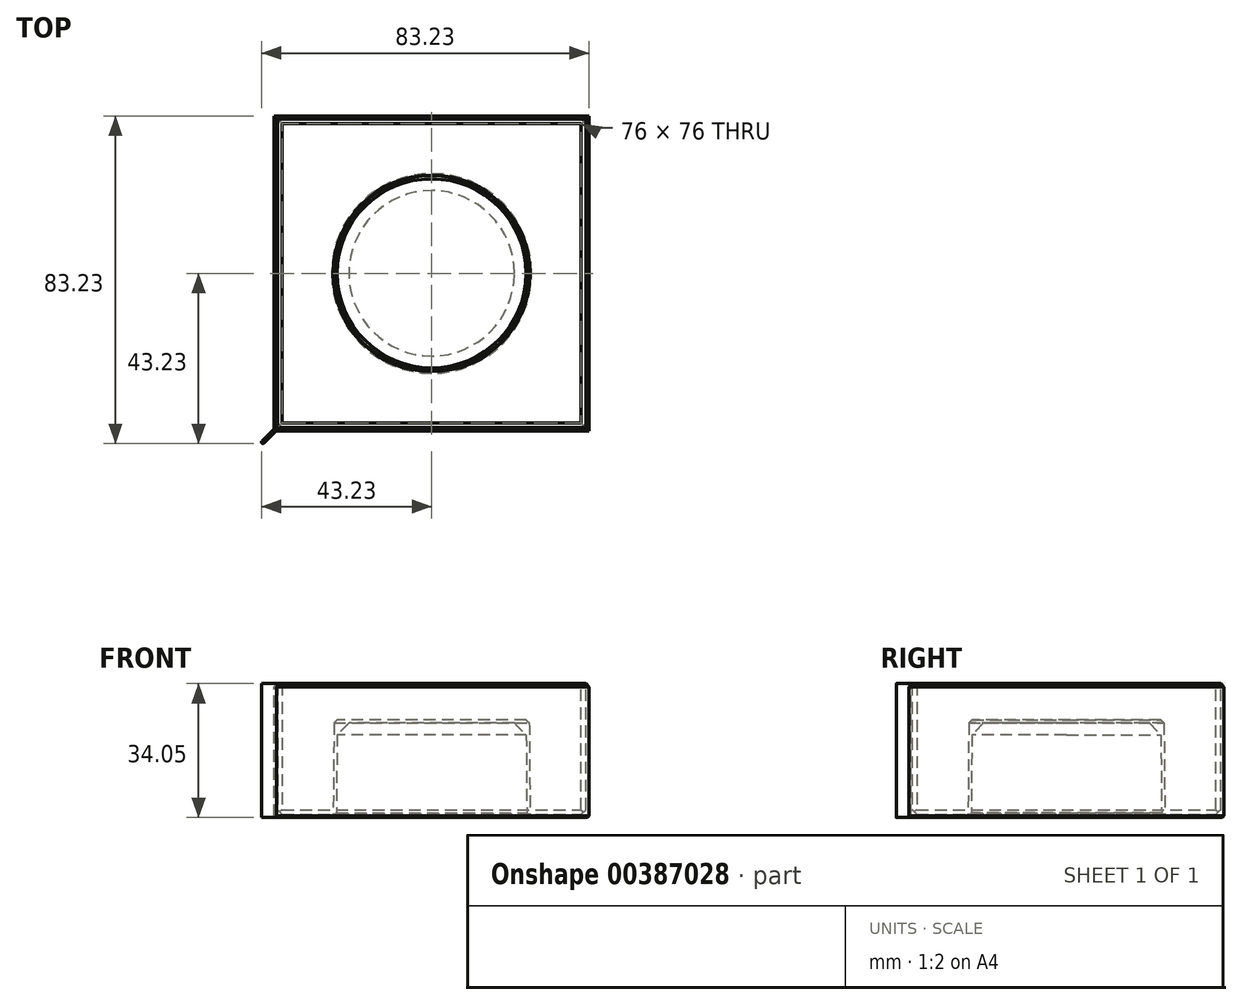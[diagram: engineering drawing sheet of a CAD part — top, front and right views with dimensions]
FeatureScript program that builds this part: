
annotation { "Feature Type Name" : "Feature", "Feature Type Description" : "" }
export const myFeature = defineFeature(function(context is Context, id is Id, definition is map)
    precondition{}
    {
        {
            var Q0;
            Q0=qCreatedBy(makeId("Top.planeOp"),FACE);
            var sketch = newSketch(context, id + "F0", { "sketchPlane" : qUnion([Q0])});
            skLineSegment(sketch, "E0.bottom", {"start": v(-40, 40) * mm, "end": v(40, 40) * mm});
            skLineSegment(sketch, "E0.top", {"start": v(-40, -40) * mm, "end": v(40, -40) * mm});
            skLineSegment(sketch, "E0.left", {"start": v(-40, 40) * mm, "end": v(-40, -40) * mm});
            skLineSegment(sketch, "E0.right", {"start": v(40, 40) * mm, "end": v(40, -40) * mm});
            skPoint(sketch, "E0.middle", {"position": v(0, 0) * mm});
            skSolve(sketch);
        }
        {
            var Q0;
            Q0 = qSketchRegion(id + "F0", true);
            extrude(context, id + "F1", {"entities" : qUnion([Q0]), "depth" : 34 * mm});
        }
        {
            var Q0;
            Q0=makeQuery(id+"F1.opExtrude","CAP_FACE",FACE,{"disambiguationData":[OSD([sQuery(id+"F0.wireOp",EDGE,"E0.bottom"),sQuery(id+"F0.wireOp",EDGE,"E0.top"),sQuery(id+"F0.wireOp",EDGE,"E0.left"),sQuery(id+"F0.wireOp",EDGE,"E0.right")])],"isStart":false});
            shell(context, id + "F2", {"entities" : qUnion([Q0]), "thickness" : 0.8 * mm});
        }
        {
            var Q0;
            Q0=makeQuery(id+"F2.opShell","OFFSET_FACE",FACE,{"disambiguationData":[OSD([sQuery(id+"F0.wireOp",EDGE,"E0.bottom"),sQuery(id+"F0.wireOp",EDGE,"E0.top"),sQuery(id+"F0.wireOp",EDGE,"E0.left"),sQuery(id+"F0.wireOp",EDGE,"E0.right")])]});
            var sketch = newSketch(context, id + "F3", { "sketchPlane" : qUnion([Q0])});
            skCircle(sketch, "E1", {"center": v(0, 0) * mm, "radius": 25 * mm});
            skSolve(sketch);
        }
        {
            var Q0;
            Q0 = qSketchRegion(id + "F3", true);
            extrude(context, id + "F4", {"entities" : qUnion([Q0]), "operationType" : NewBodyOperationType.ADD, "depth" : 24 * mm, "hasDraft" : true, "draftAngle" : 0.5 * degree, "draftPullDirection" : true});
        }
        {
            var Q0;
            {var subQ0=sQuery(id+"F0.wireOp",EDGE,"E0.left");Q0=makeQuery(id+"F2.opShell","OFFSET_EDGE",EDGE,{"disambiguationData":[OSD([subQ0]),TDD([makeQuery(id+"F1.opExtrude","CAP_EDGE",EDGE,{"disambiguationData":[OSD([subQ0])],"isStart":true})])]});}
            var Q1;
            {var subQ0=sQuery(id+"F0.wireOp",EDGE,"E0.top");Q1=makeQuery(id+"F2.opShell","OFFSET_EDGE",EDGE,{"disambiguationData":[OSD([subQ0]),TDD([makeQuery(id+"F1.opExtrude","CAP_EDGE",EDGE,{"disambiguationData":[OSD([subQ0])],"isStart":true})])]});}
            var Q2;
            {var subQ0=sQuery(id+"F0.wireOp",EDGE,"E0.bottom");Q2=makeQuery(id+"F2.opShell","OFFSET_EDGE",EDGE,{"disambiguationData":[OSD([subQ0]),TDD([makeQuery(id+"F1.opExtrude","CAP_EDGE",EDGE,{"disambiguationData":[OSD([subQ0])],"isStart":true})])]});}
            var Q3;
            {var subQ0=sQuery(id+"F0.wireOp",EDGE,"E0.right");Q3=makeQuery(id+"F2.opShell","OFFSET_EDGE",EDGE,{"disambiguationData":[OSD([subQ0]),TDD([makeQuery(id+"F1.opExtrude","CAP_EDGE",EDGE,{"disambiguationData":[OSD([subQ0])],"isStart":true})])]});}
            var Q4;
            Q4=makeQuery(id+"F4.opExtrude","CAP_EDGE",EDGE,{"disambiguationData":[OSD([sQuery(id+"F3.wireOp",EDGE,"E1")])],"isStart":true});
            chamfer(context, id + "F5", {"entities" : qUnion([Q0, Q1, Q2, Q3, Q4]), "width" : 1.2 * mm, "tangentPropagation" : true});
        }
        {
            var Q0;
            Q0=makeQuery(id+"F1.opExtrude","CAP_FACE",FACE,{"disambiguationData":[OSD([sQuery(id+"F0.wireOp",EDGE,"E0.bottom"),sQuery(id+"F0.wireOp",EDGE,"E0.top"),sQuery(id+"F0.wireOp",EDGE,"E0.left"),sQuery(id+"F0.wireOp",EDGE,"E0.right")])],"isStart":false});
            var sketch = newSketch(context, id + "F6", { "sketchPlane" : qUnion([Q0])});
            skLineSegment(sketch, "E2.0.0", {"start": v(-40, 40) * mm, "end": v(-40, -40) * mm});
            skLineSegment(sketch, "E2.0.1", {"start": v(-40, -40) * mm, "end": v(40, -40) * mm});
            skLineSegment(sketch, "E2.0.2", {"start": v(40, -40) * mm, "end": v(40, 40) * mm});
            skLineSegment(sketch, "E2.0.3", {"start": v(40, 40) * mm, "end": v(-40, 40) * mm});
            skLineSegment(sketch, "E3.bottom", {"start": v(-38, -38) * mm, "end": v(38, -38) * mm});
            skLineSegment(sketch, "E3.top", {"start": v(-38, 38) * mm, "end": v(38, 38) * mm});
            skLineSegment(sketch, "E3.left", {"start": v(-38, -38) * mm, "end": v(-38, 38) * mm});
            skLineSegment(sketch, "E3.right", {"start": v(38, -38) * mm, "end": v(38, 38) * mm});
            skPoint(sketch, "E3.middle", {"position": v(0, 0) * mm});
            skSolve(sketch);
        }
        {
            var Q0;
            Q0 = qSketchRegion(id + "F6", true);
            extrude(context, id + "F7", {"entities" : qUnion([Q0]), "operationType" : NewBodyOperationType.ADD, "depth" : 0.05 * mm});
        }
        {
            var Q0;
            {var subQ0=sQuery(id+"F0.wireOp",EDGE,"E0.top");Q0=makeQuery(id+"F2.opShell","OFFSET_EDGE",EDGE,{"disambiguationData":[OSD([subQ0]),TDD([makeQuery(id+"F1.opExtrude","CAP_EDGE",EDGE,{"disambiguationData":[OSD([subQ0])],"isStart":false})])]});}
            var Q1;
            {var subQ0=sQuery(id+"F0.wireOp",EDGE,"E0.left");Q1=makeQuery(id+"F2.opShell","OFFSET_EDGE",EDGE,{"disambiguationData":[OSD([subQ0]),TDD([makeQuery(id+"F1.opExtrude","CAP_EDGE",EDGE,{"disambiguationData":[OSD([subQ0])],"isStart":false})])]});}
            var Q2;
            Q2=makeQuery(id+"F2.opShell","OFFSET_EDGE",EDGE,{"disambiguationData":[OSD([sQuery(id+"F0.wireOp",EDGE,"E0.top"),sQuery(id+"F0.wireOp",EDGE,"E0.left")])]});
            var Q3;
            Q3=makeQuery(id+"F2.opShell","OFFSET_EDGE",EDGE,{"disambiguationData":[OSD([sQuery(id+"F0.wireOp",EDGE,"E0.bottom"),sQuery(id+"F0.wireOp",EDGE,"E0.left")])]});
            var Q4;
            {var subQ0=sQuery(id+"F0.wireOp",EDGE,"E0.bottom");Q4=makeQuery(id+"F2.opShell","OFFSET_EDGE",EDGE,{"disambiguationData":[OSD([subQ0]),TDD([makeQuery(id+"F1.opExtrude","CAP_EDGE",EDGE,{"disambiguationData":[OSD([subQ0])],"isStart":false})])]});}
            var Q5;
            {var subQ0=sQuery(id+"F0.wireOp",EDGE,"E0.right");Q5=makeQuery(id+"F2.opShell","OFFSET_EDGE",EDGE,{"disambiguationData":[OSD([subQ0]),TDD([makeQuery(id+"F1.opExtrude","CAP_EDGE",EDGE,{"disambiguationData":[OSD([subQ0])],"isStart":false})])]});}
            var Q6;
            Q6=makeQuery(id+"F2.opShell","OFFSET_EDGE",EDGE,{"disambiguationData":[OSD([sQuery(id+"F0.wireOp",EDGE,"E0.bottom"),sQuery(id+"F0.wireOp",EDGE,"E0.right")])]});
            var Q7;
            Q7=makeQuery(id+"F2.opShell","OFFSET_EDGE",EDGE,{"disambiguationData":[OSD([sQuery(id+"F0.wireOp",EDGE,"E0.top"),sQuery(id+"F0.wireOp",EDGE,"E0.right")])]});
            chamfer(context, id + "F8", {"entities" : qUnion([Q0, Q1, Q2, Q3, Q4, Q5, Q6, Q7]), "width" : 1.2 * mm, "tangentPropagation" : true});
        }
        {
            var Q0;
            Q0=makeQuery(id+"F4.opExtrude","CAP_EDGE",EDGE,{"disambiguationData":[OSD([sQuery(id+"F3.wireOp",EDGE,"E1")])],"isStart":false});
            chamfer(context, id + "F9", {"entities" : qUnion([Q0]), "width" : 0.8 * mm, "tangentPropagation" : true});
        }
        {
            var Q0;
            Q0=makeQuery(id+"F1.opExtrude","CAP_FACE",FACE,{"disambiguationData":[OSD([sQuery(id+"F0.wireOp",EDGE,"E0.bottom"),sQuery(id+"F0.wireOp",EDGE,"E0.top"),sQuery(id+"F0.wireOp",EDGE,"E0.left"),sQuery(id+"F0.wireOp",EDGE,"E0.right")])],"isStart":true});
            var sketch = newSketch(context, id + "F10", { "sketchPlane" : qUnion([Q0])});
            skLineSegment(sketch, "E4", {"start": v(-40, 40) * mm, "end": v(-42.83, 42.83) * mm});
            skArc(sketch, "E5.0.startCap", {"start": v(-39.72, 40.28) * mm, "mid": v(-39.72, 39.72) * mm, "end": v(-40.28, 39.72) * mm});
            skArc(sketch, "E5.0.endCap", {"start": v(-43.11, 42.55) * mm, "mid": v(-43.11, 43.11) * mm, "end": v(-42.55, 43.11) * mm});
            skLineSegment(sketch, "E5.0.left", {"start": v(-40.28, 39.72) * mm, "end": v(-43.11, 42.55) * mm});
            skLineSegment(sketch, "E5.0.right", {"start": v(-39.72, 40.28) * mm, "end": v(-42.55, 43.11) * mm});
            skLineSegment(sketch, "E6", {"start": v(-40.28, 39.72) * mm, "end": v(-39.73, 39.16) * mm});
            skLineSegment(sketch, "E7", {"start": v(-39.73, 39.16) * mm, "end": v(-39.16, 39.73) * mm});
            skLineSegment(sketch, "E8", {"start": v(-39.72, 40.28) * mm, "end": v(-39.16, 39.73) * mm});
            skSolve(sketch);
        }
        {
            var Q0;
            Q0 = qSketchRegion(id + "F10", true);
            var Q1;
            Q1=makeQuery(id+"F7.opExtrude","CAP_FACE",FACE,{"disambiguationData":[OSD([sQuery(id+"F6.wireOp",EDGE,"E2.0.0"),sQuery(id+"F6.wireOp",EDGE,"E2.0.1"),sQuery(id+"F6.wireOp",EDGE,"E2.0.2"),sQuery(id+"F6.wireOp",EDGE,"E2.0.3"),sQuery(id+"F6.wireOp",EDGE,"E3.bottom"),sQuery(id+"F6.wireOp",EDGE,"E3.top"),sQuery(id+"F6.wireOp",EDGE,"E3.left"),sQuery(id+"F6.wireOp",EDGE,"E3.right")])],"isStart":false});
            extrude(context, id + "F11", {"entities" : qUnion([Q0]), "operationType" : NewBodyOperationType.ADD, "endBound" : BoundingType.UP_TO_SURFACE, "oppositeDirection" : true, "endBoundEntityFace" : qUnion([Q1]), "depth" : 25 * mm});
        }
        {
            var Q0;
            Q0=qCreatedBy(makeId("Front.planeOp"),FACE);
            var sketch = newSketch(context, id + "F12", { "sketchPlane" : qUnion([Q0])});
            skLineSegment(sketch, "E9", {"start": v(-25.05, -4.73) * mm, "end": v(-24.79, 25.01) * mm});
            skLineSegment(sketch, "E10.0", {"start": v(-24.23, -2.24) * mm, "end": v(-24, 24) * mm});
            skLineSegment(sketch, "E11.0", {"start": v(24.8, 24) * mm, "end": v(-24.8, 24) * mm});
            skLineSegment(sketch, "E12", {"start": v(-24.23, -2.24) * mm, "end": v(0, -2.24) * mm});
            skLineSegment(sketch, "E13", {"start": v(0, -2.24) * mm, "end": v(0, 24) * mm});
            skSolve(sketch);
        }
        {
            var Q0;
            Q0 = qSketchRegion(id + "F12", true);
            var Q1;
            Q1=sQuery(id+"F12.wireOp",EDGE,"E13");
            revolve(context, id + "F13", {"operationType" : NewBodyOperationType.REMOVE, "entities" : qUnion([Q0]), "axis" : qUnion([Q1]), "revolveType" : RevolveType.FULL, "oppositeDirection" : true});
        }
        {
            var Q0;
            Q0=makeQuery(id+"F13.boolean.opBoolean","COPY",EDGE,{"derivedFrom":makeQuery(id+"F13.opRevolve","SWEPT_EDGE",EDGE,{"disambiguationData":[OSD([sQuery(id+"F12.wireOp",EDGE,"E10.0"),sQuery(id+"F12.wireOp",EDGE,"E11.0")])]})});
            chamfer(context, id + "F14", {"entities" : qUnion([Q0]), "width" : 3 * mm, "tangentPropagation" : true});
        }
        {
            var Q0;
            {var subQ0=sQuery(id+"F10.wireOp",EDGE,"E8");var subQ1=sQuery(id+"F10.wireOp",EDGE,"E7");var subQ2=sQuery(id+"F10.wireOp",EDGE,"E6");var subQ3=sQuery(id+"F10.wireOp",EDGE,"E5.0.right");var subQ4=sQuery(id+"F10.wireOp",EDGE,"E5.0.left");var subQ5=sQuery(id+"F10.wireOp",EDGE,"E5.0.endCap");Q0=makeQuery(id+"F13.boolean.opBoolean","INTERSECT",EDGE,{"derivedFrom":[makeQuery(id+"FufW74rbtwLAsxb_1.3.F11.boolean.opBoolean","MERGE",FACE,{"derivedFrom":[makeQuery(id+"FufW74rbtwLAsxb_1.2.F11.boolean.opBoolean","MERGE",FACE,{"derivedFrom":[makeQuery(id+"FufW74rbtwLAsxb_1.1.F11.boolean.opBoolean","MERGE",FACE,{"derivedFrom":[makeQuery(id+"F11.boolean.opBoolean","MERGE",FACE,{"derivedFrom":[makeQuery(id+"F1.opExtrude","CAP_FACE",FACE,{"disambiguationData":[OSD([sQuery(id+"F0.wireOp",EDGE,"E0.bottom"),sQuery(id+"F0.wireOp",EDGE,"E0.top"),sQuery(id+"F0.wireOp",EDGE,"E0.left"),sQuery(id+"F0.wireOp",EDGE,"E0.right")])],"isStart":true}),makeQuery(id+"F11.opExtrude","CAP_FACE",FACE,{"disambiguationData":[OSD([subQ5,subQ4,subQ3,subQ2,subQ1,subQ0])],"isStart":true})]}),makeQuery(id+"FufW74rbtwLAsxb_1.1.F11.opExtrude","CAP_FACE",FACE,{"disambiguationData":[OSD([subQ5,subQ4,subQ3,subQ2,subQ1,subQ0])],"isStart":true})]}),makeQuery(id+"FufW74rbtwLAsxb_1.2.F11.opExtrude","CAP_FACE",FACE,{"disambiguationData":[OSD([subQ5,subQ4,subQ3,subQ2,subQ1,subQ0])],"isStart":true})]}),makeQuery(id+"FufW74rbtwLAsxb_1.3.F11.opExtrude","CAP_FACE",FACE,{"disambiguationData":[OSD([subQ5,subQ4,subQ3,subQ2,subQ1,subQ0])],"isStart":true})]}),makeQuery(id+"F13.opRevolve","SWEPT_FACE",FACE,{"disambiguationData":[OSD([sQuery(id+"F12.wireOp",EDGE,"E10.0")])]})]});}
            chamfer(context, id + "F15", {"entities" : qUnion([Q0]), "width" : 1.2 * mm, "tangentPropagation" : true});
        }
        {
            var Q0;
            Q0=makeQuery(id+"F1.opExtrude","CAP_EDGE",EDGE,{"disambiguationData":[OSD([sQuery(id+"F0.wireOp",EDGE,"E0.top")])],"isStart":true});
            var Q1;
            Q1=makeQuery(id+"F1.opExtrude","CAP_EDGE",EDGE,{"disambiguationData":[OSD([sQuery(id+"F0.wireOp",EDGE,"E0.left")])],"isStart":true});
            var Q2;
            Q2=makeQuery(id+"F1.opExtrude","CAP_EDGE",EDGE,{"disambiguationData":[OSD([sQuery(id+"F0.wireOp",EDGE,"E0.right")])],"isStart":true});
            var Q3;
            Q3=makeQuery(id+"F1.opExtrude","CAP_EDGE",EDGE,{"disambiguationData":[OSD([sQuery(id+"F0.wireOp",EDGE,"E0.bottom")])],"isStart":true});
            chamfer(context, id + "F16", {"entities" : qUnion([Q0, Q1, Q2, Q3]), "width" : 0.4 * mm, "tangentPropagation" : true});
        }
        {
            var Q0;
            Q0=makeQuery(id+"F7.opExtrude","CAP_EDGE",EDGE,{"disambiguationData":[OSD([sQuery(id+"F6.wireOp",EDGE,"E2.0.1")])],"isStart":false});
            var Q1;
            Q1=makeQuery(id+"F7.opExtrude","CAP_EDGE",EDGE,{"disambiguationData":[OSD([sQuery(id+"F6.wireOp",EDGE,"E2.0.2")])],"isStart":false});
            var Q2;
            Q2=makeQuery(id+"F7.opExtrude","CAP_EDGE",EDGE,{"disambiguationData":[OSD([sQuery(id+"F6.wireOp",EDGE,"E2.0.3")])],"isStart":false});
            var Q3;
            Q3=makeQuery(id+"F7.opExtrude","CAP_EDGE",EDGE,{"disambiguationData":[OSD([sQuery(id+"F6.wireOp",EDGE,"E2.0.0")])],"isStart":false});
            chamfer(context, id + "F17", {"entities" : qUnion([Q0, Q1, Q2, Q3]), "width" : 0.8 * mm, "tangentPropagation" : true});
        }
    });
